FCSTD DOCUMENT  (FreeCAD 0.16R6712 (Git))
Label: MT_master_cad 1
License: All rights reserved
LicenseURL: http://en.wikipedia.org/wiki/All_rights_reserved
objects: Part::Feature×32, Part::FeaturePython×15, App::DocumentObjectGroup×8, Part::Cylinder×7, Part::Compound×7, Sketcher::SketchObject×1, PartDesign::Pad×1
note: 64 computed .brp shape members not serialized (recipe doc carries the construction recipe); baked Part::Feature solids carry a one-line shape summary decoded from their .brp

FEATURE [Part::Feature] Pad005  label="Idler Mount Front Right"
  Placement = pos=(-4.40597,1414.4,-575.391) rot=(1,0,0;1.5708rad)
  shape: bbox 203.2 x 10 x 215.9 mm, 9 faces (baked)
FEATURE [Part::Feature] Pad006  label="Idler Mount Front Left"
  Placement = pos=(-4.4001,1932.4,-575.391) rot=(1,0,0;1.5708rad)
  shape: bbox 203.2 x 10 x 215.9 mm, 9 faces (baked)
FEATURE [Part::Cylinder] Cylinder  label="Shaft Rear"
  Angle = 360
  Height = 1066.8
  Placement = pos=(-919.053,2201.93,-708.8) rot=(1,0,0;1.5708rad)
  Radius = 38.1
FEATURE [Part::Cylinder] Cylinder001  label="Shaft Front"
  Angle = 360
  Height = 1066.8
  Placement = pos=(-4.5503,2202.18,-708.745) rot=(1,0,0;1.5708rad)
  Radius = 38.1
FEATURE [Part::Cylinder] Cylinder009  label="Loader Shaft"
  Angle = 360
  Height = 1066.8
  Placement = pos=(-766.4,2202.18,-99.2001) rot=(1,0,0;1.5708rad)
  Radius = 36.5125
FEATURE [Part::Feature] Cylinder013  label="Loader Cylinder Pivot"
  Placement = pos=(147.32,2149.65,-429.26) rot=(1,0,0;1.5708rad)
  shape: bbox 50.8 x 965.2 x 50.8 mm, 3 faces (baked)
FEATURE [Part::Cylinder] Cylinder014  label="Person"
  Angle = 360
  Height = 1524
  Placement = pos=(-1660.29,1661.1,-878.529) rot=(0,0,1;0rad)
  Radius = 254
FEATURE [Part::Feature] Box  label="PowerCube"
  Placement = pos=(-715.6,1414.4,-556.4) rot=(0,0,1;0rad)
  shape: bbox 762 x 508 x 508 mm, 6 faces (baked)
FEATURE [Sketcher::SketchObject] Sketch001
  Placement = pos=(-1272.29,1414.4,-383.553) rot=(0.57735,-0.57735,-0.57735;2.0944rad)
  sketch-geometry (4):
    g0: LineSegment StartX=-504.052 StartY=503.704 StartZ=0 EndX=-2.4e-05 EndY=503.704 EndZ=0
    g1: LineSegment StartX=-2.4e-05 StartY=503.704 StartZ=0 EndX=-2.4e-05 EndY=-9e-06 EndZ=0
    g2: LineSegment StartX=-2.4e-05 StartY=-9e-06 StartZ=0 EndX=-504.052 EndY=-9e-06 EndZ=0
    g3: LineSegment StartX=-504.052 StartY=-9e-06 StartZ=0 EndX=-504.052 EndY=503.704 EndZ=0
  constraints (8):
    c: Coincident(g0,g1)
    c: Coincident(g1,g2)
    c: Coincident(g2,g3)
    c: Coincident(g3,g0)
    c: Horizontal(g0)
    c: Horizontal(g2)
    c: Vertical(g1)
    c: Vertical(g3)
FEATURE [PartDesign::Pad] Pad025  label="Pad033"
  Length = 457.2
  Length2 = 100
  Placement = pos=(-1272.29,1414.4,-383.553) rot=(0.57735,-0.57735,-0.57735;2.0944rad)
  Reversed = true
  Sketch = -> Sketch001
  Type = 0
FEATURE [Part::FeaturePython] Washer  label="M6-Washer"  # Fasteners workbench fastener (typed FeaturePython)
  Placement = pos=(-257.748,1462.43,-664.207) rot=(0,0,1;0rad)
  diameter = 2
  invert = false
  matchOuter = false
  offset = 0
  type = 4
FEATURE [Part::FeaturePython] Washer001  label="M6-Washer007"  # Fasteners workbench fastener (typed FeaturePython)
  Placement = pos=(-260.35,1877.04,-552.45) rot=(0,0,1;0rad)
  diameter = 2
  invert = false
  matchOuter = false
  offset = 0
  type = 4
FEATURE [Part::FeaturePython] Washer002  label="M6-Washer009"  # Fasteners workbench fastener (typed FeaturePython)
  Placement = pos=(-260.35,1877.04,-664.207) rot=(0,0,1;0rad)
  diameter = 2
  invert = false
  matchOuter = false
  offset = 0
  type = 4
FEATURE [Part::FeaturePython] Washer003  label="M6-Washer008"  # Fasteners workbench fastener (typed FeaturePython)
  Placement = pos=(-257.748,1462.43,-552.45) rot=(0,0,1;0rad)
  diameter = 2
  invert = false
  matchOuter = false
  offset = 0
  type = 4
FEATURE [Part::FeaturePython] Screw  label="M6x120-Screw"  # Fasteners workbench fastener (typed FeaturePython)
  Placement = pos=(-257.748,1462.43,-549.9) rot=(0,0,1;0rad)
  diameter = 8
  invert = false
  length = 12
  matchOuter = false
  offset = 0
  thread = false
  type = 13
FEATURE [Part::FeaturePython] Screw001  label="M6x120-Screw001"  # Fasteners workbench fastener (typed FeaturePython)
  Placement = pos=(-260.35,1877.04,-549.9) rot=(0,0,1;0rad)
  diameter = 8
  invert = false
  length = 12
  matchOuter = false
  offset = 0
  thread = false
  type = 13
FEATURE [Part::FeaturePython] Washer004  label="M10-Washer"  # Fasteners workbench fastener (typed FeaturePython)
  Placement = pos=(-257.748,1462.43,-661.907) rot=(0,0,1;0rad)
  diameter = 4
  invert = false
  matchOuter = false
  offset = 0
  type = 4
FEATURE [Part::FeaturePython] Washer005  label="M10-Washer001"  # Fasteners workbench fastener (typed FeaturePython)
  Placement = pos=(-260.35,1877.04,-661.667) rot=(0,0,1;0rad)
  diameter = 4
  invert = false
  matchOuter = false
  offset = 0
  type = 4
FEATURE [Part::FeaturePython] Nut  label="M6-Nut"  # Fasteners workbench fastener (typed FeaturePython)
  Placement = pos=(-257.748,1462.43,-663.587) rot=(1,0,0;3.14159rad)
  diameter = 2
  invert = false
  matchOuter = false
  offset = 0
  thread = false
  type = 2
FEATURE [Part::FeaturePython] Nut001  label="M6-Nut001"  # Fasteners workbench fastener (typed FeaturePython)
  Placement = pos=(-260.35,1877.04,-663.587) rot=(1,0,0;3.14159rad)
  diameter = 2
  invert = false
  matchOuter = false
  offset = 0
  thread = false
  type = 2
FEATURE [Part::Compound] Compound017  label="PC1708"
  Placement = pos=(-622.3,1308.1,0) rot=(0,0,1;0rad)
FEATURE [Part::Compound] Compound018  label="clamp Loader right"
  Placement = pos=(-766.4,1059.18,-99.2001) rot=(1,0,0;1.5708rad)
FEATURE [Part::Compound] Compound019  label="clamp Loader left"
  Placement = pos=(-766.4,2278.38,-99.2001) rot=(-1,0,0;1.5708rad)
FEATURE [Part::Compound] Compound020  label="clamp shaft front left"
  Placement = pos=(-4.4001,1693.8,-708.745) rot=(1,0,0;1.5708rad)
FEATURE [Part::Compound] Compound021  label="clamp shaft front right"
  Placement = pos=(-4.40003,1643,-708.745) rot=(-1,0,0;1.5708rad)
FEATURE [Part::Compound] Compound022  label="clamp shaft rear right"
  Placement = pos=(-919.053,1643,-708.8) rot=(-1,0,0;1.5708rad)
FEATURE [Part::Compound] Compound025  label="clamp shaft rear left"
  Placement = pos=(-918.865,1998.6,-708.8) rot=(-1,0,0;1.5708rad)
FEATURE [App::DocumentObjectGroup] Group010  label="Shafts"
  Group = -> [Cylinder013,Cylinder009]
FEATURE [Part::Cylinder] Cylinder054  label="Shaft Arms 1"
  Angle = 360
  Height = 584.2
  Placement = pos=(195.079,1960.88,-268.24) rot=(1,0,0;1.5708rad)
  Radius = 50.8
FEATURE [Part::Cylinder] Cylinder055  label="Shaft Arms 2"
  Angle = 360
  Height = 584.2
  Placement = pos=(-354.271,1960.88,785.767) rot=(1,0,0;1.5708rad)
  Radius = 50.8
FEATURE [Part::Feature] Fusion001  label="QA Cylinder retr. R"
  Placement = pos=(-1387.75,5.61326,-3873.86) rot=(0.833126,0.548547,-0.070692;1.40232rad)
  shape: bbox 541.7 x 50.8 x 330.8 mm, 39 faces (baked)
FEATURE [Part::Feature] Fusion002001  label="QA Cylinder ext. R"
  Placement = pos=(1104.89,-4639.21,-2200.88) rot=(0.899609,-0.130856,0.416631;1.15054rad)
  shape: bbox 806.5 x 50.8 x 481.8 mm, 38 faces (baked)
FEATURE [Part::Feature] Fusion002002  label="QA Cylinder retr. L"
  Placement = pos=(-1387.75,729.513,-3873.86) rot=(0.833126,0.548547,-0.070692;1.40232rad)
  shape: bbox 541.7 x 50.8 x 330.8 mm, 39 faces (baked)
FEATURE [Part::Feature] Fusion002003  label="QA Cylinder ext. L"
  Placement = pos=(1104.89,-3915.31,-2200.88) rot=(0.899609,-0.130856,0.416631;1.15054rad)
  shape: bbox 806.5 x 50.8 x 481.8 mm, 38 faces (baked)
FEATURE [Part::Feature] Pad026  label="Idler Mount Rear Right"
  Placement = pos=(-919.053,1414.4,-575.45) rot=(1,0,0;1.5708rad)
  shape: bbox 203.2 x 10 x 215.9 mm, 9 faces (baked)
FEATURE [Part::Feature] Pad027  label="Idler Mount Rear Left"
  Placement = pos=(-919.053,1932.4,-575.45) rot=(1,0,0;1.5708rad)
  shape: bbox 203.2 x 10 x 215.9 mm, 9 faces (baked)
FEATURE [Part::Feature] Fusion002006  label="Arm cylinder retr. R"
  Placement = pos=(0,10.16,0) rot=(0,0,1;0rad)
  shape: bbox 621.5 x 77.62 x 324 mm, 12 faces (baked)
FEATURE [Part::Feature] Fusion002007001  label="Arm cylinder retr. L"
  Placement = pos=(0,-13.462,0) rot=(0,0,1;0rad)
  shape: bbox 621.5 x 77.62 x 324 mm, 12 faces (baked)
FEATURE [Part::Feature] Fusion002007002  label="Arm Cylinder ext. R"
  Placement = pos=(0,9.652,0) rot=(0,0,1;0rad)
  shape: bbox 819.8 x 77.62 x 693.1 mm, 12 faces (baked)
FEATURE [Part::Feature] Fusion002007003  label="Arm Cylinder ext. L"
  Placement = pos=(0,733.552,0) rot=(0,0,1;0rad)
  shape: bbox 819.8 x 77.62 x 693.1 mm, 12 faces (baked)
FEATURE [Part::FeaturePython] Nut003  label="M30-Nut019"  # Fasteners workbench fastener (typed FeaturePython)
  Placement = pos=(-766.312,1668.34,-196.481) rot=(0,0,1;0rad)
  diameter = 19
  invert = false
  matchOuter = false
  offset = 0
  thread = false
  type = 1
FEATURE [Part::Cylinder] Cylinder056  label="Threaded 1 in rod"
  Angle = 360
  Height = 279.4
  Placement = pos=(-766.312,1668.34,-427.113) rot=(0,0,1;0rad)
  Radius = 12.7
FEATURE [Part::FeaturePython] Nut004  label="M30-Nut"  # Fasteners workbench fastener (typed FeaturePython)
  Placement = pos=(-766.312,1668.34,-396.811) rot=(0,0,1;0rad)
  diameter = 19
  invert = false
  matchOuter = false
  offset = 0
  thread = false
  type = 1
FEATURE [Part::Feature] Compound010003  label="Idler Front Right"
  Placement = pos=(51.403,1092.95,-860.194) rot=(0,0,1;3.14159rad)
  shape: bbox 302.3 x 217 x 302.3 mm, 148 faces, 13 solids (baked)
FEATURE [Part::Feature] Compound004001  label="Idler Rear Left"
  Placement = pos=(-974.857,2245.2,-860.249) rot=(0,0,1;0rad)
  shape: bbox 302.3 x 217 x 302.3 mm, 148 faces, 13 solids (baked)
FEATURE [Part::Feature] Compound003001  label="Idler Front Left"
  Placement = pos=(-60.3537,2245.2,-860.194) rot=(0,0,1;0rad)
  shape: bbox 302.3 x 217 x 302.3 mm, 148 faces, 13 solids (baked)
FEATURE [Part::Feature] Compound002001  label="Idler Rear Right"
  Placement = pos=(-863.25,1092.95,-860.249) rot=(0,0,1;3.14159rad)
  shape: bbox 302.3 x 217 x 302.3 mm, 148 faces, 13 solids (baked)
FEATURE [Part::Feature] Compound001  label="15.9 cu in motor right"
  Placement = pos=(-697.185,1307.52,-338.452) rot=(0,1,0;3.14159rad)
  shape: bbox 248.4 x 213.9 x 248.4 mm, 198 faces, 8 solids (baked)
FEATURE [Part::Feature] Part__Mirroring002  label="15.9 cu in motor left"
  Placement = pos=(-1676.25,3335.98,-856.696) rot=(0,1,0;3.14159rad)
  shape: bbox 248.4 x 213.9 x 248.4 mm, 198 faces, 8 solids (baked)
FEATURE [Part::Feature] PathArray001  label="Track right"
  Placement = pos=(0,8.255,0) rot=(0,0,1;0rad)
  shape: bbox 1356 x 228.6 x 625.7 mm, 4536 faces, 294 solids (baked)
FEATURE [Part::Feature] PathArray002  label="Track left"
  Placement = pos=(0,846.455,0) rot=(0,0,1;0rad)
  shape: bbox 1356 x 228.6 x 625.7 mm, 4536 faces, 294 solids (baked)
FEATURE [App::DocumentObjectGroup] Group004  label="Drive Train"
  Group = -> [Compound010003,Compound004001,Compound002001,Compound003001,PathArray001,PathArray002]
FEATURE [Part::Feature] Fusion004003002002003004  label="Small PC"
  Placement = pos=(-1458.91,1306.45,0) rot=(0,0,1;0rad)
  shape: bbox 457.5 x 508 x 501.7 mm, 390 faces, 5 solids (baked)
FEATURE [App::DocumentObjectGroup] Group005  label="Power"
  Group = -> [Box,Pad025,Compound017,Washer,Washer001,Washer002,Washer003,Screw,Screw001,Washer004,Washer005,Nut,Nut001,Fusion004003002002003004]
FEATURE [Part::Feature] Pocket003003  label="Pocket003"
  Placement = pos=(-766.4,1605.28,-99.2001) rot=(-1,0,0;1.5708rad)
  shape: bbox 101.6 x 127 x 101.6 mm, 4 faces (baked)
FEATURE [Part::FeaturePython] Nut005  label="M30-Nut018"  # Fasteners workbench fastener (typed FeaturePython)
  Placement = pos=(-766.312,1668.87,-170.573) rot=(0,0,1;0rad)
  diameter = 19
  invert = false
  matchOuter = false
  offset = 0
  thread = false
  type = 1
FEATURE [Part::Feature] Pocket003005001  label="Tensioner assembly"
  Placement = pos=(-605.263,1033.73,-429.722) rot=(0,0,1;0rad)
  shape: bbox 165.1 x 647.1 x 139.7 mm, 88 faces (baked)
FEATURE [App::DocumentObjectGroup] Group011  label="Tensioner"
  Group = -> [Nut003,Cylinder056,Nut004,Part__Mirroring002,Compound001,Pocket003005001,Nut005,Pocket003003]
FEATURE [Part::Feature] Compound010004  label="Lowered Arm R"
  Placement = pos=(-422.344,2172.03,548.89) rot=(0,0,1;0rad)
  shape: bbox 1227 x 139.7 x 690.6 mm, 34 faces, 2 solids (baked)
FEATURE [Part::Feature] Compound010005  label="Lowered Arm L"
  Placement = pos=(-422.344,2895.93,548.89) rot=(0,0,1;0rad)
  shape: bbox 1227 x 139.7 x 690.6 mm, 34 faces, 2 solids (baked)
FEATURE [Part::Feature] Compound010006  label="Raised Arm R"
  Placement = pos=(-1303.36,2172.03,400.871) rot=(0,-1,0;1.309rad)
  shape: bbox 962.1 x 139.7 x 1034 mm, 34 faces, 2 solids (baked)
FEATURE [Part::Feature] Compound010007  label="Raised Arm L"
  Placement = pos=(-1303.36,2895.93,400.871) rot=(0,-1,0;1.309rad)
  shape: bbox 962.1 x 139.7 x 1034 mm, 34 faces, 2 solids (baked)
FEATURE [Part::FeaturePython] Clone001  label="1 hole tubing"  # WARN: FeaturePython — macro-defined, semantics opaque (R4)
  Placement = pos=(148,1465.2,-556.22) rot=(0,0,1;0rad)
  Scale = (1,1,1)
FEATURE [Part::FeaturePython] Clone002  label="1 hole tubing001"  # WARN: FeaturePython — macro-defined, semantics opaque (R4)
  Placement = pos=(148,1871.6,-556.22) rot=(0,0,1;0rad)
  Scale = (1,1,1)
FEATURE [Part::Feature] Fillet002  label="Bucket +QA lowered"
  Placement = pos=(536.923,2202.18,-857.073) rot=(0,-1,0;0.1309rad)
  shape: bbox 913 x 1067 x 513 mm, 515 faces, 10 solids (baked)
FEATURE [App::DocumentObjectGroup] Group009  label="Lowered Arm"
  Group = -> [Cylinder054,Fusion002002,Fusion001,Fusion002006,Fusion002007001,Compound010005,Compound010004,Fillet002]
FEATURE [Part::Feature] Fillet001001  label="Bucket +QA raised"
  Placement = pos=(194.431,2202.18,619.622) rot=(0,1,0;0.270526rad)
  shape: bbox 808.5 x 1067 x 689.3 mm, 515 faces, 10 solids (baked)
FEATURE [App::DocumentObjectGroup] Group001  label="Raised Arm"
  Group = -> [Cylinder055,Fusion002001,Fusion002003,Fusion002007002,Fusion002007003,Compound010006,Compound010007,Fillet001001]
FEATURE [App::DocumentObjectGroup] Group006  label="Loader"
  Group = -> [Group001,Group009,Group010]
FEATURE [Part::Feature] MT_Frame_02001  label="Frame Stock Tube"
  Placement = pos=(-1122,1465.2,-607.141) rot=(0,0,1;0rad)
  shape: bbox 1321 x 508 x 609.6 mm, 206 faces (baked)
FEATURE [App::DocumentObjectGroup] Group003  label="Frame"
  Group = -> [Cylinder,Cylinder001,Compound021,Compound022,Compound020,Compound019,Compound018,Compound025,Pad005,Pad006,Pad026,Pad027,Clone001,Clone002,MT_Frame_02001]
